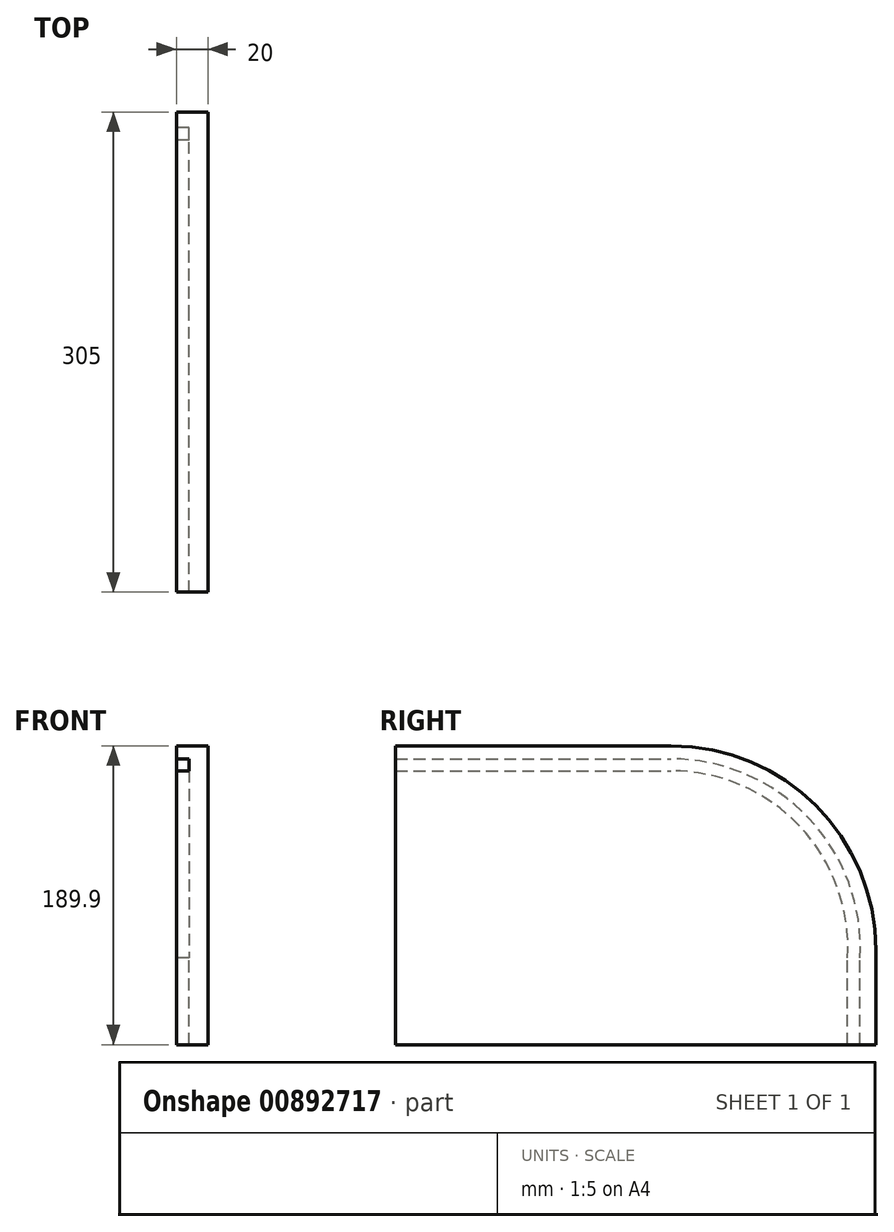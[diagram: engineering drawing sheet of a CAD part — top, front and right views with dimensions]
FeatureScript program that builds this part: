
annotation { "Feature Type Name" : "Feature", "Feature Type Description" : "" }
export const myFeature = defineFeature(function(context is Context, id is Id, definition is map)
    precondition{}
    {
        {
            var Q0;
            Q0=qCreatedBy(makeId("Right.planeOp"),FACE);
            var sketch = newSketch(context, id + "F0", { "sketchPlane" : qUnion([Q0])});
            skLineSegment(sketch, "E0", {"start": v(-175, 76.78) * mm, "end": v(-175, -113.12) * mm});
            skLineSegment(sketch, "E1", {"start": v(-175, -113.12) * mm, "end": v(130, -113.12) * mm});
            skLineSegment(sketch, "E2", {"start": v(130, -113.12) * mm, "end": v(130, -53.12) * mm});
            skLineSegment(sketch, "E3", {"start": v(-175, 76.78) * mm, "end": v(0, 76.78) * mm});
            skArc(sketch, "E4", {"start": v(130, -53.12) * mm, "mid": v(91.89, 38.74) * mm, "end": v(0, 76.78) * mm});
            skSolve(sketch);
        }
        {
            var Q0;
            Q0=makeQuery(id+"F0.imprint","IMPRINT",FACE,{"disambiguationData":[TD([[makeQuery(id+"F0.imprint","IMPRINT",EDGE,{"derivedFrom":sQuery(id+"F0.wireOp",EDGE,"E0")}),1.0]])]});
            extrude(context, id + "F1", {"entities" : qUnion([Q0]), "depth" : 20 * mm, "offsetDistance" : 25 * mm});
        }
        {
            var Q0;
            Q0=makeQuery(id+"F1.opExtrude","CAP_FACE",FACE,{"disambiguationData":[OSD([sQuery(id+"F0.wireOp",EDGE,"E0"),sQuery(id+"F0.wireOp",EDGE,"E1"),sQuery(id+"F0.wireOp",EDGE,"E2"),sQuery(id+"F0.wireOp",EDGE,"E3"),sQuery(id+"F0.wireOp",EDGE,"E4")])],"isStart":true});
            var sketch = newSketch(context, id + "F2", { "sketchPlane" : qUnion([Q0])});
            skLineSegment(sketch, "E5", {"start": v(175, 68.41) * mm, "end": v(0, 68.41) * mm});
            skLineSegment(sketch, "E6", {"start": v(175, 60.81) * mm, "end": v(0, 60.81) * mm});
            skLineSegment(sketch, "E7", {"start": v(-120, -113.12) * mm, "end": v(-120, -58.12) * mm});
            skLineSegment(sketch, "E8", {"start": v(-112, -113.12) * mm, "end": v(-112, -58.12) * mm});
            skArc(sketch, "E9", {"start": v(0, 60.81) * mm, "mid": v(-81.68, 25.53) * mm, "end": v(-112, -58.12) * mm});
            skArc(sketch, "E10", {"start": v(0, 68.41) * mm, "mid": v(-87.2, 30.94) * mm, "end": v(-120, -58.12) * mm});
            skSolve(sketch);
        }
        {
            var Q0;
            Q0 = qSketchRegion(id + "F2", true);
            var Q1;
            {var subQ4=sQuery(id+"F2.wireOp",EDGE,"E5");Q1=makeQuery(id+"F2.imprint","IMPRINT",FACE,{"disambiguationData":[TD([[makeQuery(id+"F2.imprint","IMPRINT",EDGE,{"derivedFrom":subQ4}),1.0]])]});}
            extrude(context, id + "F3", {"entities" : qUnion([Q0, Q1]), "operationType" : NewBodyOperationType.REMOVE, "oppositeDirection" : true, "depth" : 8 * mm, "offsetDistance" : 25 * mm});
        }
    });
